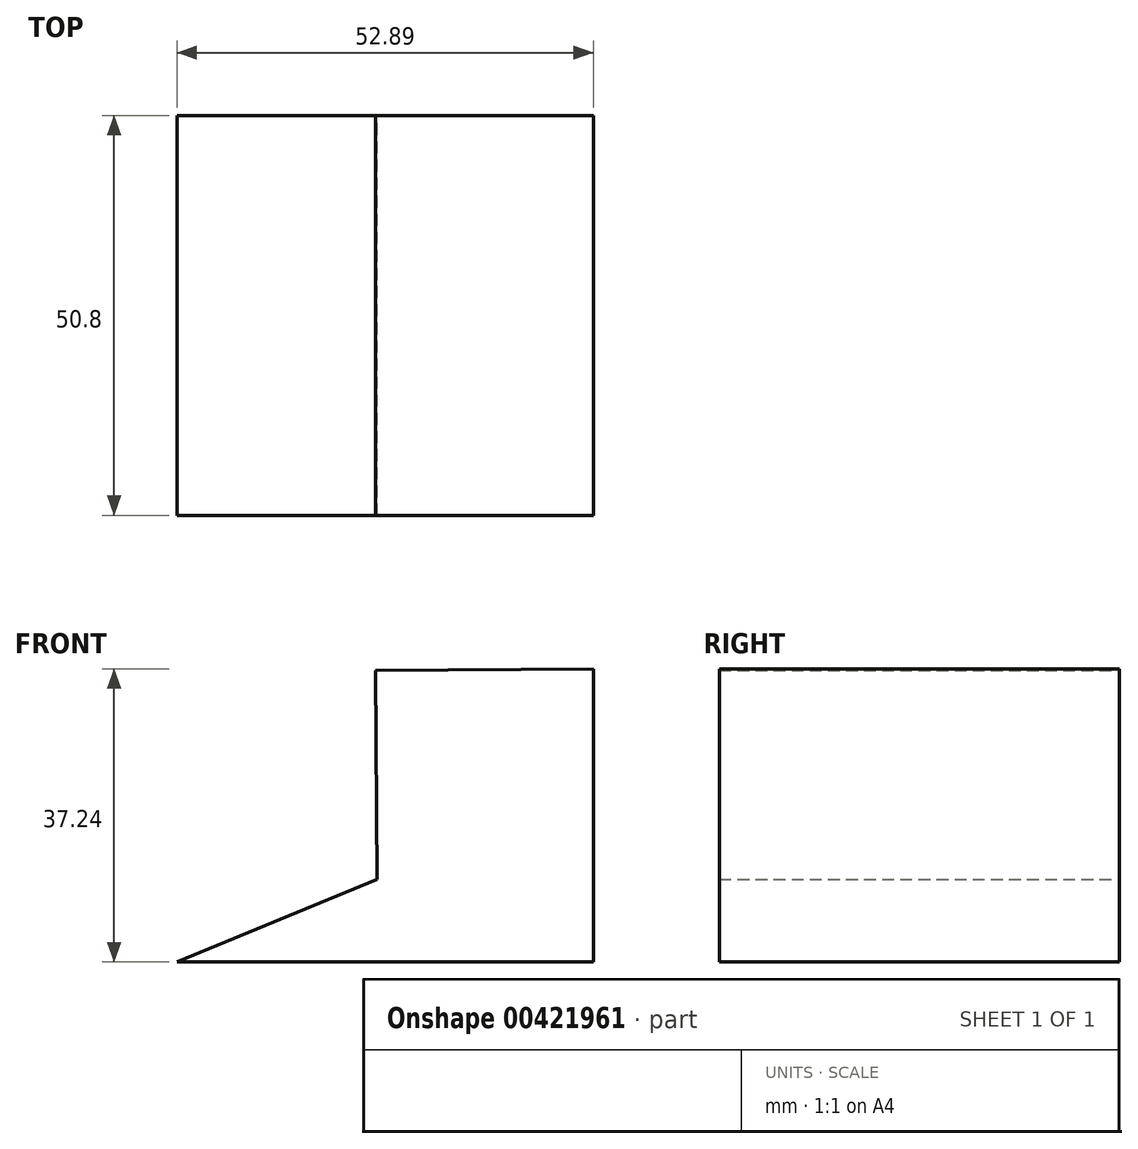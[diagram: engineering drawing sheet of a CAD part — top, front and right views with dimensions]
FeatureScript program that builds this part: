
annotation { "Feature Type Name" : "Feature", "Feature Type Description" : "" }
export const myFeature = defineFeature(function(context is Context, id is Id, definition is map)
    precondition{}
    {
        {
            var Q0;
            Q0=qCreatedBy(makeId("Front.planeOp"),FACE);
            var sketch = newSketch(context, id + "F0", { "sketchPlane" : qUnion([Q0])});
            skLineSegment(sketch, "E0", {"start": v(0, 0) * mm, "end": v(-52.9, 0) * mm});
            skLineSegment(sketch, "E1", {"start": v(-52.9, 0) * mm, "end": v(-27.5, 10.5) * mm});
            skLineSegment(sketch, "E2", {"start": v(-27.5, 10.5) * mm, "end": v(-27.69, 37.05) * mm});
            skLineSegment(sketch, "E3", {"start": v(-27.69, 37.05) * mm, "end": v(0, 37.24) * mm});
            skLineSegment(sketch, "E4", {"start": v(0, 37.24) * mm, "end": v(0, 0) * mm});
            skSolve(sketch);
        }
        {
            var Q0;
            Q0=makeQuery(id+"F0.imprint","IMPRINT",FACE,{"disambiguationData":[TD([[makeQuery(id+"F0.imprint","IMPRINT",EDGE,{"derivedFrom":sQuery(id+"F0.wireOp",EDGE,"E0")}),-1.0]])]});
            extrude(context, id + "F1", {"entities" : qUnion([Q0]), "depth" : 50.8 * mm});
        }
    });
